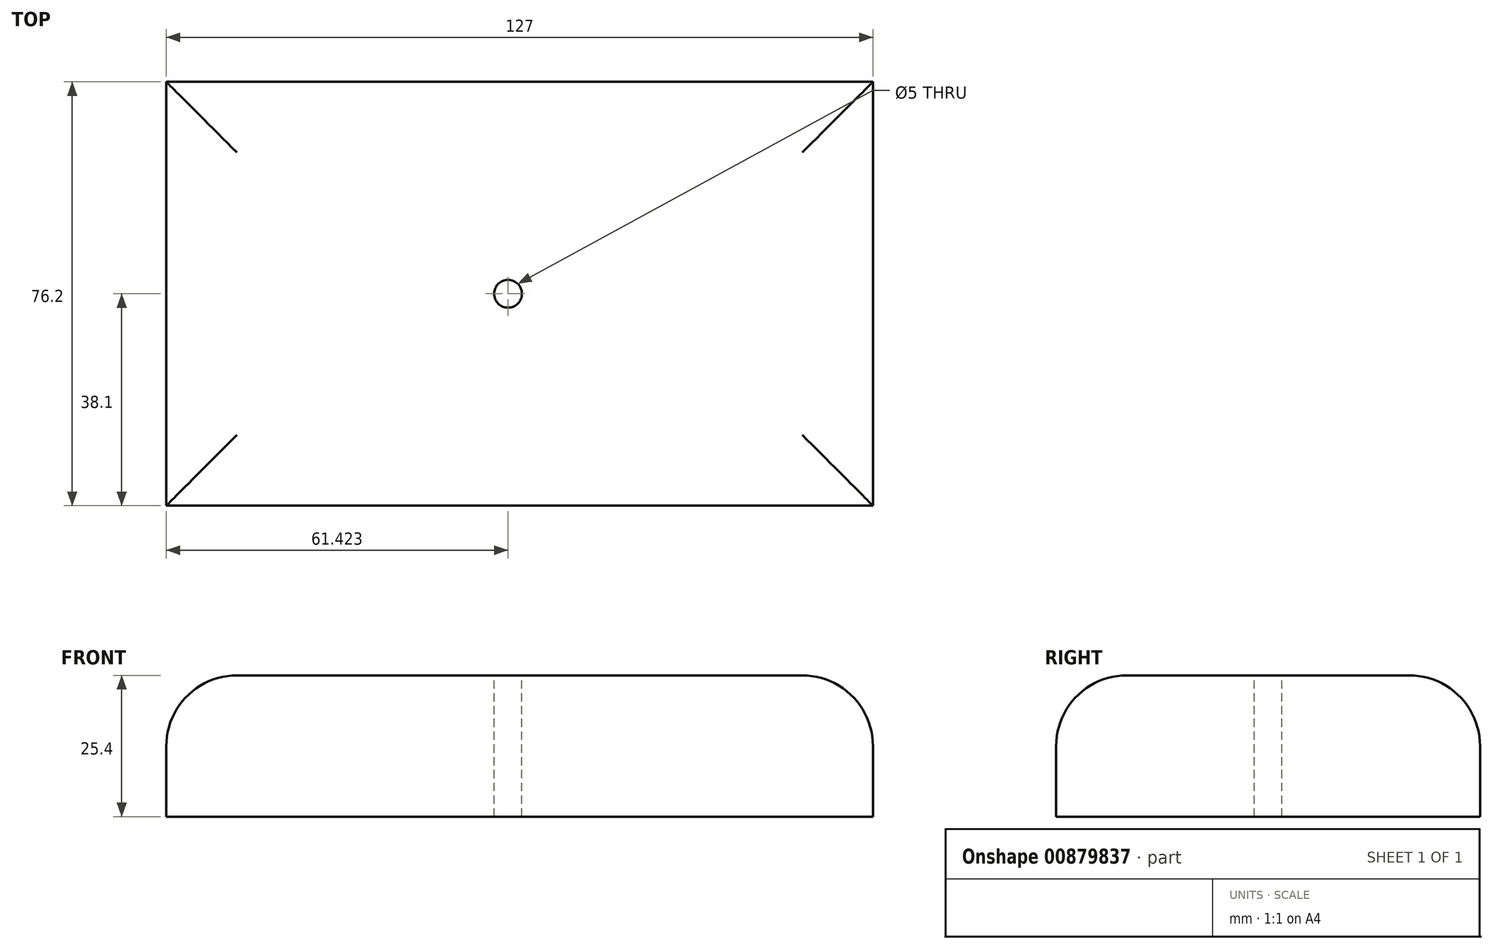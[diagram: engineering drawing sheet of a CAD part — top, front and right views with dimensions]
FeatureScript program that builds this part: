
annotation { "Feature Type Name" : "Feature", "Feature Type Description" : "" }
export const myFeature = defineFeature(function(context is Context, id is Id, definition is map)
    precondition{}
    {
        {
            var Q0;
            Q0=qCreatedBy(makeId("Top.planeOp"),FACE);
            var sketch = newSketch(context, id + "F0", { "sketchPlane" : qUnion([Q0])});
            skLineSegment(sketch, "E0.bottom", {"start": v(63.5, 38.1) * mm, "end": v(-63.5, 38.1) * mm});
            skLineSegment(sketch, "E0.top", {"start": v(63.5, -38.1) * mm, "end": v(-63.5, -38.1) * mm});
            skLineSegment(sketch, "E0.left", {"start": v(63.5, 38.1) * mm, "end": v(63.5, -38.1) * mm});
            skLineSegment(sketch, "E0.right", {"start": v(-63.5, 38.1) * mm, "end": v(-63.5, -38.1) * mm});
            skPoint(sketch, "E0.middle", {"position": v(0, 0) * mm});
            skSolve(sketch);
        }
        {
            var Q0;
            Q0 = qSketchRegion(id + "F0", true);
            extrude(context, id + "F1", {"entities" : qUnion([Q0]), "depth" : 25.4 * mm, "offsetDistance" : 25.4 * mm});
        }
        {
            var Q0;
            Q0=makeQuery(id+"F1.opExtrude","CAP_FACE",FACE,{"disambiguationData":[OSD([sQuery(id+"F0.wireOp",EDGE,"E0.bottom"),sQuery(id+"F0.wireOp",EDGE,"E0.top"),sQuery(id+"F0.wireOp",EDGE,"E0.left"),sQuery(id+"F0.wireOp",EDGE,"E0.right")])],"isStart":false});
            var sketch = newSketch(context, id + "F2", { "sketchPlane" : qUnion([Q0])});
            skCircle(sketch, "E1", {"center": v(-2.08, 0) * mm, "radius": 2.5 * mm});
            skSolve(sketch);
        }
        {
            var Q0;
            Q0 = qSketchRegion(id + "F2", true);
            extrude(context, id + "F3", {"entities" : qUnion([Q0]), "operationType" : NewBodyOperationType.REMOVE, "oppositeDirection" : true, "depth" : 25.4 * mm, "offsetDistance" : 25.4 * mm});
        }
        {
            var Q0;
            Q0=makeQuery(id+"F1.opExtrude","CAP_EDGE",EDGE,{"disambiguationData":[OSD([sQuery(id+"F0.wireOp",EDGE,"E0.left")])],"isStart":false});
            var Q1;
            Q1=makeQuery(id+"F1.opExtrude","CAP_EDGE",EDGE,{"disambiguationData":[OSD([sQuery(id+"F0.wireOp",EDGE,"E0.bottom")])],"isStart":false});
            var Q2;
            Q2=makeQuery(id+"F1.opExtrude","CAP_EDGE",EDGE,{"disambiguationData":[OSD([sQuery(id+"F0.wireOp",EDGE,"E0.top")])],"isStart":false});
            var Q3;
            Q3=makeQuery(id+"F1.opExtrude","CAP_EDGE",EDGE,{"disambiguationData":[OSD([sQuery(id+"F0.wireOp",EDGE,"E0.right")])],"isStart":false});
            fillet(context, id + "F4", {"entities" : qUnion([Q0, Q1, Q2, Q3]), "radius" : 12.7 * mm, "tangentPropagation" : true, "allowEdgeOverflow" : false});
        }
    });
